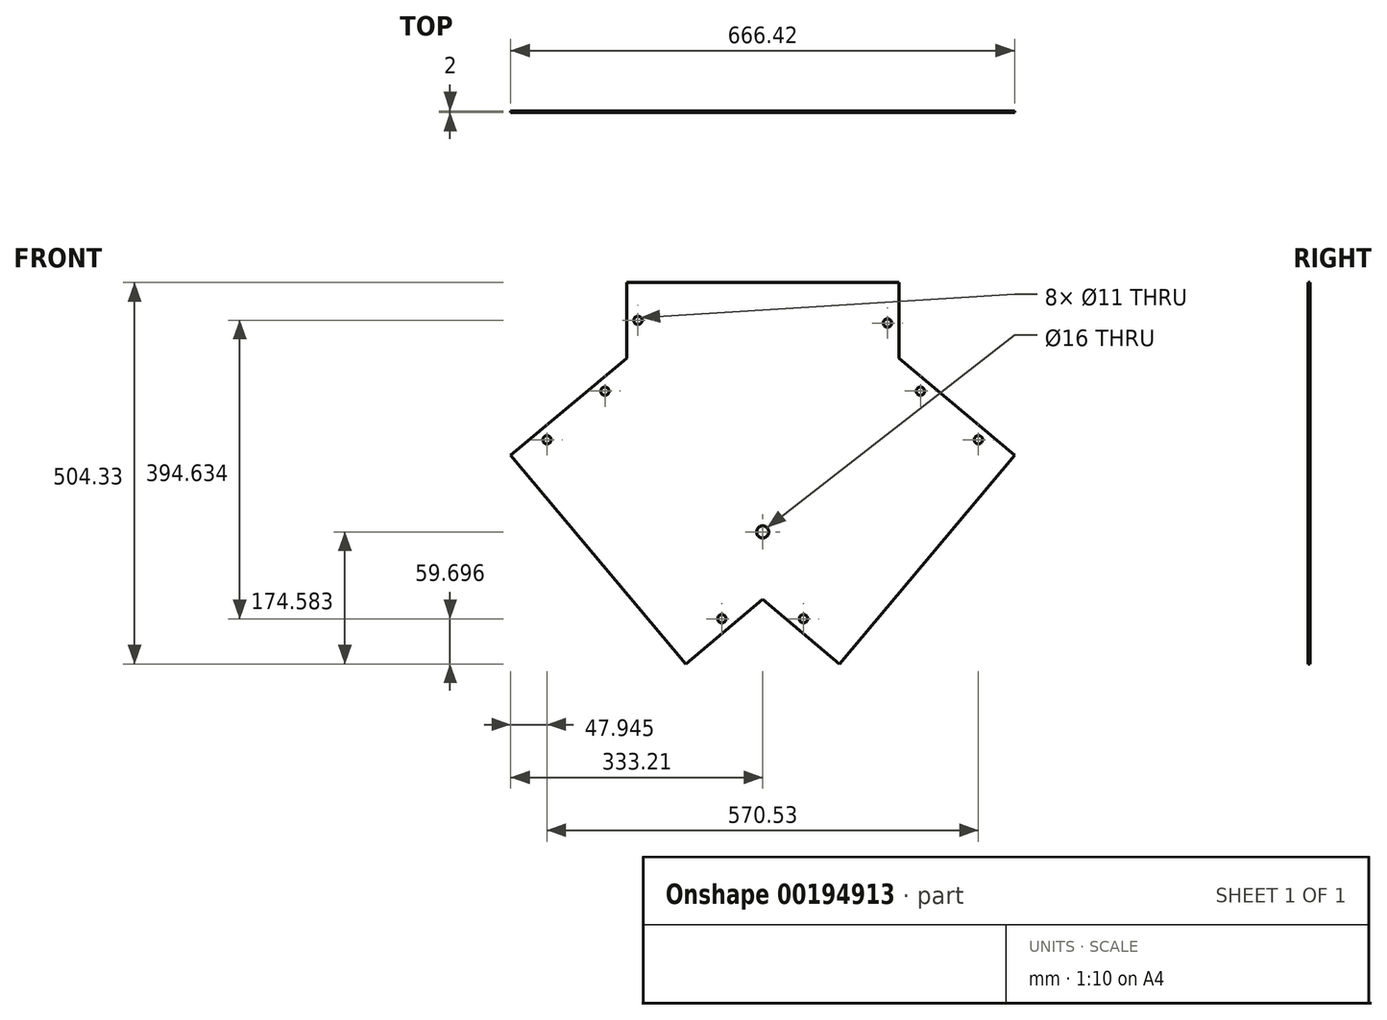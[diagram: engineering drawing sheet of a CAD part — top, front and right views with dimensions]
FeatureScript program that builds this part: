
annotation { "Feature Type Name" : "Feature", "Feature Type Description" : "" }
export const myFeature = defineFeature(function(context is Context, id is Id, definition is map)
    precondition{}
    {
        {
            var Q0;
            Q0=qCreatedBy(makeId("Front.planeOp"),FACE);
            var sketch = newSketch(context, id + "F0", { "sketchPlane" : qUnion([Q0])});
            skLineSegment(sketch, "E0", {"start": v(0, 0) * mm, "end": v(180, 0) * mm});
            skLineSegment(sketch, "E1", {"start": v(180, 0) * mm, "end": v(180, -100) * mm});
            skLineSegment(sketch, "E2", {"start": v(180, -100) * mm, "end": v(333.2, -228.56) * mm});
            skLineSegment(sketch, "E3", {"start": v(333.2, -228.56) * mm, "end": v(101.8, -504.33) * mm});
            skLineSegment(sketch, "E4", {"start": v(101.8, -504.33) * mm, "end": v(0, -418.9) * mm});
            skLineSegment(sketch, "E5", {"start": v(0, -418.9) * mm, "end": v(-101.8, -504.33) * mm});
            skLineSegment(sketch, "E6", {"start": v(-101.8, -504.33) * mm, "end": v(-333.2, -228.56) * mm});
            skLineSegment(sketch, "E7", {"start": v(-333.2, -228.56) * mm, "end": v(-180, -100) * mm});
            skLineSegment(sketch, "E8", {"start": v(-180, -100) * mm, "end": v(-180, 0) * mm});
            skLineSegment(sketch, "E9", {"start": v(-180, 0) * mm, "end": v(0, 0) * mm});
            skLineSegment(sketch, "E10", {"start": v(-150, 0) * mm, "end": v(-150, -113.99) * mm, "construction": true});
            skLineSegment(sketch, "E11", {"start": v(-150, -113.99) * mm, "end": v(-313.93, -251.54) * mm, "construction": true});
            skLineSegment(sketch, "E12", {"start": v(-121.09, -481.35) * mm, "end": v(0, -379.75) * mm, "construction": true});
            skLineSegment(sketch, "E13", {"start": v(0, -379.75) * mm, "end": v(121.09, -481.35) * mm, "construction": true});
            skLineSegment(sketch, "E14", {"start": v(313.93, -251.54) * mm, "end": v(150, -113.99) * mm, "construction": true});
            skLineSegment(sketch, "E15", {"start": v(150, -113.99) * mm, "end": v(150, 0) * mm, "construction": true});
            skLineSegment(sketch, "E16", {"start": v(-323.57, -240.05) * mm, "end": v(-165, -107) * mm, "construction": true});
            skLineSegment(sketch, "E17", {"start": v(-165, -107) * mm, "end": v(-165, 0) * mm, "construction": true});
            skLineSegment(sketch, "E18", {"start": v(165, 0) * mm, "end": v(165, -107) * mm, "construction": true});
            skLineSegment(sketch, "E19", {"start": v(165, -107) * mm, "end": v(323.57, -240.05) * mm, "construction": true});
            skLineSegment(sketch, "E20", {"start": v(-111.45, -492.84) * mm, "end": v(0, -399.33) * mm, "construction": true});
            skLineSegment(sketch, "E21", {"start": v(0, -399.33) * mm, "end": v(111.45, -492.84) * mm, "construction": true});
            skCircle(sketch, "E22", {"center": v(-285.26, -207.9) * mm, "radius": 5.5 * mm});
            skCircle(sketch, "E23", {"center": v(-208.66, -143.63) * mm, "radius": 5.5 * mm});
            skCircle(sketch, "E24", {"center": v(208.66, -143.63) * mm, "radius": 5.5 * mm});
            skCircle(sketch, "E25", {"center": v(285.26, -207.9) * mm, "radius": 5.5 * mm});
            skCircle(sketch, "E26", {"center": v(-54, -444.63) * mm, "radius": 5.5 * mm});
            skCircle(sketch, "E27", {"center": v(54, -444.63) * mm, "radius": 5.5 * mm});
            skCircle(sketch, "E28", {"center": v(-165, -50) * mm, "radius": 5.5 * mm});
            skPoint(sketch, "E28.centerSnap0", {"position": v(-180, -50) * mm});
            skCircle(sketch, "E29", {"center": v(165, -53.5) * mm, "radius": 5.5 * mm});
            skCircle(sketch, "E30", {"center": v(0, -329.75) * mm, "radius": 8 * mm});
            skSolve(sketch);
        }
        {
            var Q0;
            Q0 = qSketchRegion(id + "F0", true);
            extrude(context, id + "F1", {"entities" : qUnion([Q0]), "oppositeDirection" : true, "depth" : 2 * mm});
        }
    });
